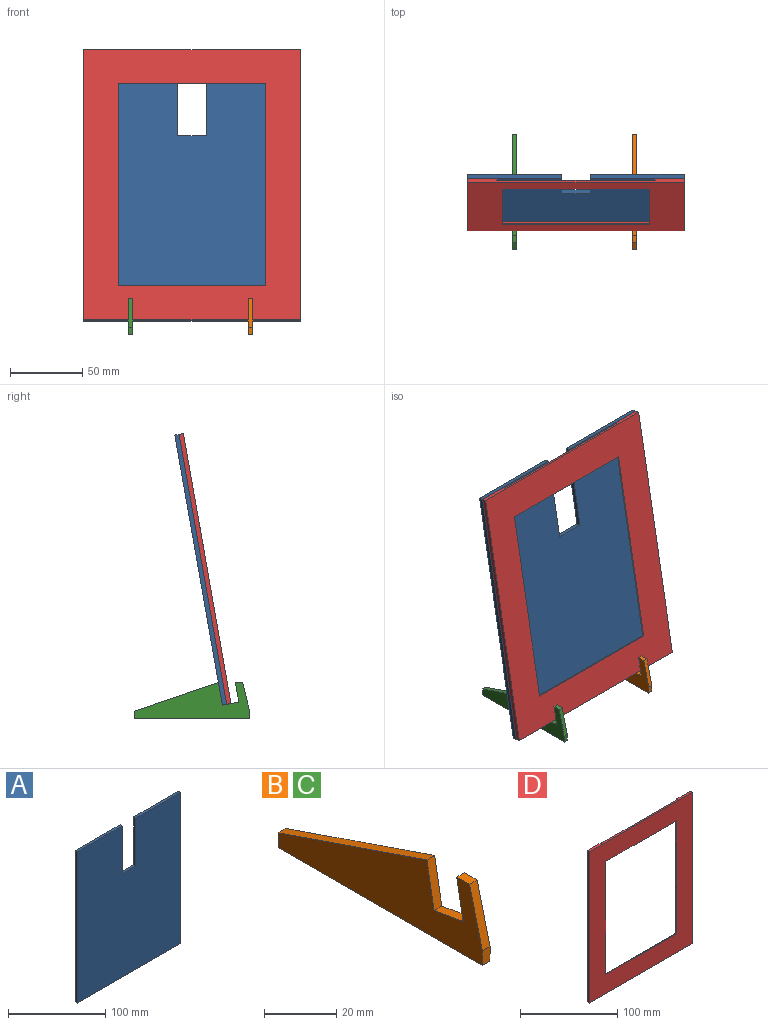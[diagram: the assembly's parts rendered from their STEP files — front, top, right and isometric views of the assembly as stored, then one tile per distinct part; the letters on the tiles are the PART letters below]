
ASSEMBLY  parts=4 mates=7
PART A: 10 faces, bbox 150x3x190 mm
  f0: plane 65x3mm, normal (0,0,1), area 195mm2, adj f1,f7,f8,f9
  f1: plane 190x3mm, normal (-1,0,0), area 570mm2, adj f0,f2,f8,f9
  f2: plane 150x3mm, normal (0,0,-1), area 450mm2, adj f1,f3,f8,f9
  f3: plane 190x3mm, normal (1,0,0), area 570mm2, adj f2,f4,f8,f9
  f4: plane 65x3mm, normal (0,0,1), area 195mm2, adj f3,f5,f8,f9
  f5: plane 60x3mm, normal (-1,0,0), area 180mm2, adj f4,f6,f8,f9
  f6: plane 20x3mm, normal (0,0,1), area 60mm2, adj f5,f7,f8,f9
  f7: plane 60x3mm, normal (1,0,0), area 180mm2, adj f0,f6,f8,f9
  f8: plane 190x150mm, normal (0,-1,0), area 27300mm2, adj f0,f1,f2,f3,f4,f5,f6,f7
  f9: plane 190x150mm, normal (0,1,0), area 27300mm2, adj f0,f1,f2,f3,f4,f5,f6,f7
PART B: 11 faces, bbox 3x80x25 mm
  f0: plane 15.78x3mm, normal (0,-0.98,0.17), area 48.1mm2, adj f1,f8,f9,f10
  f1: plane 11.33x3mm, normal (0,0.17,0.98), area 34.5mm2, adj f0,f2,f9,f10
  f2: plane 13.79x3mm, normal (0,0.98,-0.17), area 42mm2, adj f1,f3,f9,f10
  f3: plane 5x3mm, normal (0,0,1), area 15mm2, adj f2,f4,f9,f10
  f4: plane 20x5mm, normal (0,-0.97,0.24), area 61.8mm2, adj f3,f5,f9,f10
  f5: plane 5x3mm, normal (0,-1,0), area 15mm2, adj f4,f6,f9,f10
  f6: plane 80x3mm, normal (0,0,-1), area 240mm2, adj f5,f7,f9,f10
  f7: plane 5x3mm, normal (0,1,0), area 15mm2, adj f6,f8,f9,f10
  f8: plane 58.32x20mm, normal (0,0.32,0.95), area 185mm2, adj f0,f7,f9,f10
  f9: plane 80x25mm, normal (1,0,0), area 1194.1mm2, adj f0,f1,f2,f3,f4,f5,f6,f7
  f10: plane 80x25mm, normal (-1,0,0), area 1194.1mm2, adj f0,f1,f2,f3,f4,f5,f6,f7
PART C: same geometry as B
PART D: 16 faces, bbox 150x3x190 mm
  f0: plane 190x150mm, normal (0,1,0), area 9800mm2, adj f1,f6,f7,f8,f10,f12,f13
  f1: plane 150x3mm, normal (0,0,1), area 340mm2, adj f0,f6,f8,f9,f10,f12,f15
  f2: plane 142x1mm, normal (1,0,0), area 142mm2, adj f3,f5,f9,f14
  f3: plane 102x1mm, normal (0,0,-1), area 102mm2, adj f2,f4,f9,f14
  f4: plane 142x1mm, normal (-1,0,0), area 142mm2, adj f3,f5,f9,f14
  f5: plane 102x1mm, normal (0,0,1), area 102mm2, adj f2,f4,f9,f14
  f6: plane 190x3mm, normal (-1,0,0), area 570mm2, adj f0,f1,f7,f9
  f7: plane 150x3mm, normal (0,0,-1), area 450mm2, adj f0,f6,f8,f9
  f8: plane 190x3mm, normal (1,0,0), area 570mm2, adj f0,f1,f7,f9
  f9: plane 190x150mm, normal (0,-1,0), area 14016mm2, adj f1,f2,f3,f4,f5,f6,f7,f8
  f10: plane 170x2mm, normal (1,0,0), area 320mm2, adj f0,f1,f11,f13,f14,f15
  f11: plane 110x1mm, normal (0,0,-1), area 110mm2, adj f10,f12,f14,f15
  f12: plane 170x2mm, normal (-1,0,0), area 320mm2, adj f0,f1,f11,f13,f14,f15
  f13: plane 110x2mm, normal (0,0,1), area 220mm2, adj f0,f10,f12,f14
  f14: plane 150x110mm, normal (0,1,0), area 2016mm2, adj f2,f3,f4,f5,f10,f11,f12,f13
  f15: plane 110x20mm, normal (0,1,0), area 2200mm2, adj f1,f10,f11,f12
PLACE A rot(axis=(-1,0,0),10deg) t=(-42.97,24.89,172.43)mm
PLACE B t=(71.03,-27,-23.9)mm
PLACE C t=(-11.97,-27,-23.9)mm fixed
PLACE D rot(axis=(-1,0,0),10deg) t=(-18.97,17.77,149.31)mm
MATE planar D.f0 <-> A.f8  axis (0,0.98,-0.17) through (32.03,2.13,60.6)mm
MATE planar D.f7 <-> C.f1  axis (0,-0.17,-0.98) through (32.03,-12.53,-13.91)mm
MATE planar D.f1 <-> A.f0  axis (0,0.17,0.98) through (32.03,20.14,173.26)mm
MATE planar C.f4 <-> B.f4  axis (0,-0.97,0.24) through (-10.47,-24.5,-8.9)mm
MATE planar A.f9 <-> C.f0  axis (0,0.98,-0.17) through (32.03,7.9,76.06)mm
MATE planar A.f3 <-> D.f8  axis (1,0,0) through (107.03,6.92,79.13)mm
MATE parallel C.f9 <-> B.f10  axis (1,0,0) through (-8.97,8.23,-15.23)mm
